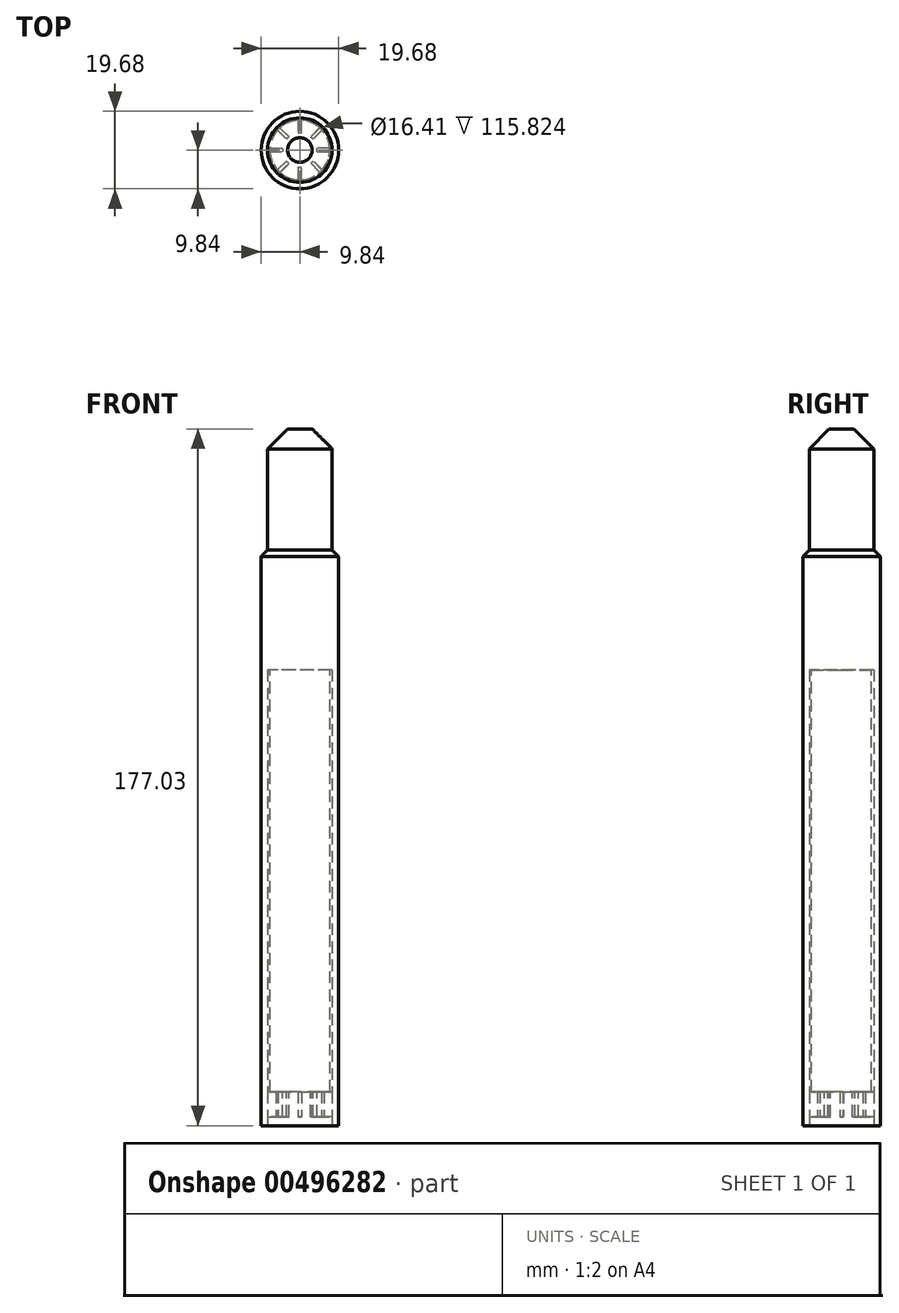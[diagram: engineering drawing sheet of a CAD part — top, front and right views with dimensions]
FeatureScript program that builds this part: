
annotation { "Feature Type Name" : "Feature", "Feature Type Description" : "" }
export const myFeature = defineFeature(function(context is Context, id is Id, definition is map)
    precondition{}
    {
        {
            var Q0;
            Q0=qCreatedBy(makeId("Top.planeOp"),FACE);
            var sketch = newSketch(context, id + "F0", { "sketchPlane" : qUnion([Q0])});
            skCircle(sketch, "E0", {"center": v(0, 0) * mm, "radius": 9.84 * mm});
            skCircle(sketch, "E1", {"center": v(0, 0) * mm, "radius": 8.2 * mm});
            skSolve(sketch);
        }
        {
            var Q0;
            Q0=makeQuery(id+"F0.imprint","IMPRINT",FACE,{"disambiguationData":[TD([[makeQuery(id+"F0.imprint","IMPRINT",EDGE,{"derivedFrom":sQuery(id+"F0.wireOp",EDGE,"E0")}),1.0]])]});
            extrude(context, id + "F1", {"entities" : qUnion([Q0]), "depth" : 25.4 * mm});
        }
        {
            var Q0;
            Q0=makeQuery(id+"F1.opExtrude","CAP_FACE",FACE,{"disambiguationData":[OSD([sQuery(id+"F0.wireOp",EDGE,"E0")])],"isStart":true});
            extrude(context, id + "F2", {"entities" : qUnion([Q0]), "operationType" : NewBodyOperationType.ADD, "depth" : 115.82 * mm});
        }
        {
            var Q0;
            Q0=makeQuery(id+"F0.imprint","IMPRINT",FACE,{"disambiguationData":[TD([[makeQuery(id+"F0.imprint","IMPRINT",EDGE,{"derivedFrom":sQuery(id+"F0.wireOp",EDGE,"E1")}),1.0]])]});
            extrude(context, id + "F3", {"entities" : qUnion([Q0]), "operationType" : NewBodyOperationType.ADD, "depth" : 61.2 * mm});
        }
        {
            var Q1;
            Q1=qCreatedBy(makeId("Origin.pointOp"),VERTEX);
            var Q2;
            Q2=makeQuery(id+"F3.opExtrude","CAP_FACE",FACE,{"disambiguationData":[OSD([sQuery(id+"F0.wireOp",EDGE,"E1")])],"isStart":false});
            loft(context, id + "F4", {"operationType" : NewBodyOperationType.ADD, "sheetProfilesArray" : [{ "sheetProfileEntities" : qUnion([Q1]) }, { "sheetProfileEntities" : qUnion([Q2]) }]});
        }
        {
            var Q0;
            Q0=qCreatedBy(makeId("Top.planeOp"),FACE);
            var sketch = newSketch(context, id + "F5", { "sketchPlane" : qUnion([Q0])});
            skCircle(sketch, "E2", {"center": v(0, 0) * mm, "radius": 7.6 * mm});
            skSolve(sketch);
        }
        {
            var Q0;
            Q0=makeQuery(id+"F3.opExtrude","SWEPT_FACE",FACE,{"disambiguationData":[OSD([sQuery(id+"F0.wireOp",EDGE,"E1")])]});
            chamfer(context, id + "F6", {"entities" : qUnion([Q0]), "width" : 5.08 * mm, "tangentPropagation" : true});
        }
        {
            var Q0;
            Q0 = qSketchRegion(id + "F5", true);
            extrude(context, id + "F7", {"entities" : qUnion([Q0]), "operationType" : NewBodyOperationType.ADD, "oppositeDirection" : true, "depth" : 107.19 * mm});
        }
        {
            var Q0;
            Q0=makeQuery(id+"F7.opExtrude","CAP_FACE",FACE,{"disambiguationData":[OSD([sQuery(id+"F5.wireOp",EDGE,"E2")])],"isStart":false});
            var sketch = newSketch(context, id + "F8", { "sketchPlane" : qUnion([Q0])});
            skLineSegment(sketch, "E3", {"start": v(-0.42, 4.36) * mm, "end": v(-0.42, 8.36) * mm});
            skLineSegment(sketch, "E4", {"start": v(-0.42, 8.36) * mm, "end": v(0.43, 8.36) * mm});
            skLineSegment(sketch, "E5", {"start": v(0.43, 8.36) * mm, "end": v(0.43, 4.36) * mm});
            skPoint(sketch, "E6.orphan", {"position": v(0, 7.6) * mm});
            skPoint(sketch, "E7.start.orphan", {"position": v(0, 2.49) * mm});
            skLineSegment(sketch, "E8", {"start": v(-0.42, 4.36) * mm, "end": v(0.43, 4.36) * mm});
            skPoint(sketch, "E9.orphan", {"position": v(0.43, 2.49) * mm});
            skLineSegment(sketch, "E10.1.0", {"start": v(-3.38, 2.78) * mm, "end": v(-2.78, 3.39) * mm});
            skLineSegment(sketch, "E10.1.1", {"start": v(-5.6, 6.22) * mm, "end": v(-2.78, 3.39) * mm});
            skLineSegment(sketch, "E10.1.2", {"start": v(-3.38, 2.78) * mm, "end": v(-6.2, 5.61) * mm});
            skLineSegment(sketch, "E10.1.3", {"start": v(-6.2, 5.61) * mm, "end": v(-5.6, 6.22) * mm});
            skLineSegment(sketch, "E10.2.0", {"start": v(-4.36, -0.42) * mm, "end": v(-4.36, 0.43) * mm});
            skLineSegment(sketch, "E10.2.1", {"start": v(-8.36, 0.43) * mm, "end": v(-4.36, 0.43) * mm});
            skLineSegment(sketch, "E10.2.2", {"start": v(-4.36, -0.42) * mm, "end": v(-8.36, -0.42) * mm});
            skLineSegment(sketch, "E10.2.3", {"start": v(-8.36, -0.42) * mm, "end": v(-8.36, 0.43) * mm});
            skLineSegment(sketch, "E10.3.0", {"start": v(-2.78, -3.38) * mm, "end": v(-3.39, -2.78) * mm});
            skLineSegment(sketch, "E10.3.1", {"start": v(-6.22, -5.6) * mm, "end": v(-3.39, -2.78) * mm});
            skLineSegment(sketch, "E10.3.2", {"start": v(-2.78, -3.38) * mm, "end": v(-5.61, -6.2) * mm});
            skLineSegment(sketch, "E10.3.3", {"start": v(-5.61, -6.2) * mm, "end": v(-6.22, -5.6) * mm});
            skLineSegment(sketch, "E10.4.0", {"start": v(0.42, -4.36) * mm, "end": v(-0.43, -4.36) * mm});
            skLineSegment(sketch, "E10.4.1", {"start": v(-0.43, -8.36) * mm, "end": v(-0.43, -4.36) * mm});
            skLineSegment(sketch, "E10.4.2", {"start": v(0.42, -4.36) * mm, "end": v(0.42, -8.36) * mm});
            skLineSegment(sketch, "E10.4.3", {"start": v(0.42, -8.36) * mm, "end": v(-0.43, -8.36) * mm});
            skLineSegment(sketch, "E10.5.0", {"start": v(3.38, -2.78) * mm, "end": v(2.78, -3.39) * mm});
            skLineSegment(sketch, "E10.5.1", {"start": v(5.6, -6.22) * mm, "end": v(2.78, -3.39) * mm});
            skLineSegment(sketch, "E10.5.2", {"start": v(3.38, -2.78) * mm, "end": v(6.2, -5.61) * mm});
            skLineSegment(sketch, "E10.5.3", {"start": v(6.2, -5.61) * mm, "end": v(5.6, -6.22) * mm});
            skLineSegment(sketch, "E10.6.0", {"start": v(4.36, 0.42) * mm, "end": v(4.36, -0.43) * mm});
            skLineSegment(sketch, "E10.6.1", {"start": v(8.36, -0.43) * mm, "end": v(4.36, -0.43) * mm});
            skLineSegment(sketch, "E10.6.2", {"start": v(4.36, 0.42) * mm, "end": v(8.36, 0.42) * mm});
            skLineSegment(sketch, "E10.6.3", {"start": v(8.36, 0.42) * mm, "end": v(8.36, -0.43) * mm});
            skLineSegment(sketch, "E10.7.0", {"start": v(2.78, 3.38) * mm, "end": v(3.39, 2.78) * mm});
            skLineSegment(sketch, "E10.7.1", {"start": v(6.22, 5.6) * mm, "end": v(3.39, 2.78) * mm});
            skLineSegment(sketch, "E10.7.2", {"start": v(2.78, 3.38) * mm, "end": v(5.61, 6.2) * mm});
            skLineSegment(sketch, "E10.7.3", {"start": v(5.61, 6.2) * mm, "end": v(6.22, 5.6) * mm});
            skPoint(sketch, "E10.center", {"position": v(0, 0) * mm});
            skSolve(sketch);
        }
        {
            var Q0;
            Q0 = qSketchRegion(id + "F8", true);
            extrude(context, id + "F9", {"entities" : qUnion([Q0]), "operationType" : NewBodyOperationType.ADD, "depth" : 6.35 * mm});
        }
    });
